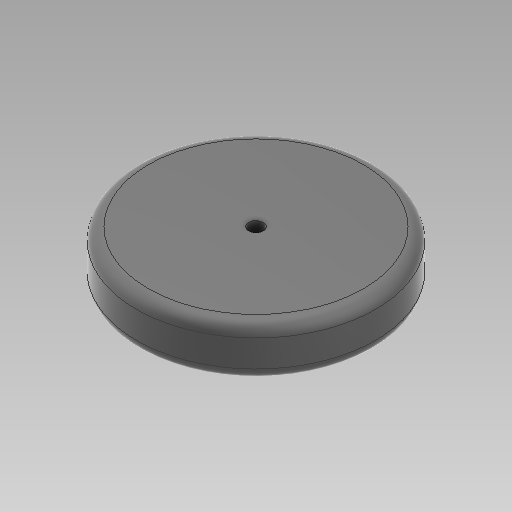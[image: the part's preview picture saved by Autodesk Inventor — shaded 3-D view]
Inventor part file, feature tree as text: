
AUTODESK INVENTOR PART (.ipt)
format: ipt  version: 2020 (Build 240168000, 168)  size: 134,144 bytes
history: native  units: in
note: dims shown in document units (in); Inventor stores cm internally (conversion verified against a paired STEP export)
features: extrude x1, fillet x1, sketch x1
ambient origin geometry x8: Origin, YZ Plane, XZ Plane, XY Plane, X Axis, Y Axis, Z Axis, Center Point
bodies: Solid1 (feature_tree)
feature tree (3):
  extrude  "Extrusion1"  Depth=0.1575in
  fillet  "Fillet1"  Radius=0.6693in
  sketch  "Sketch1"  dims[d0=3.1496in d1=0.1969in d2=0.6693in d3=0.0in d4=0.1575in]
